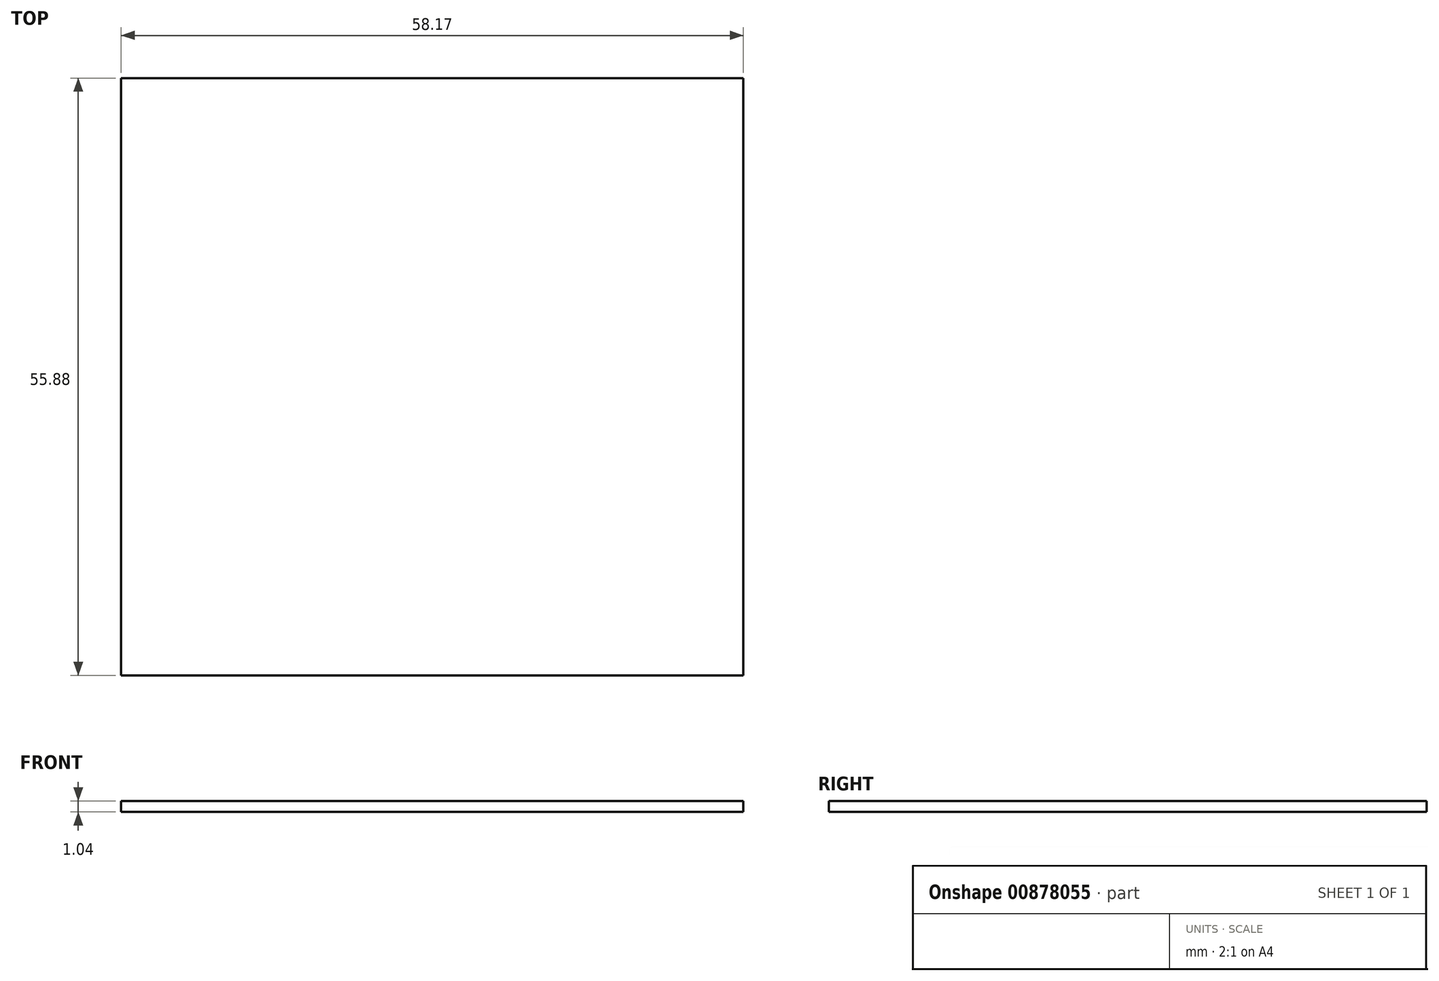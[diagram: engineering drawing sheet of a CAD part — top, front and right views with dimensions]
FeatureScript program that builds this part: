
annotation { "Feature Type Name" : "Feature", "Feature Type Description" : "" }
export const myFeature = defineFeature(function(context is Context, id is Id, definition is map)
    precondition{}
    {
        {
            var Q0;
            Q0=qCreatedBy(makeId("Top.planeOp"),FACE);
            var sketch = newSketch(context, id + "F0", { "sketchPlane" : qUnion([Q0])});
            skLineSegment(sketch, "E0.bottom", {"start": v(0, 0) * mm, "end": v(58.17, 0) * mm});
            skLineSegment(sketch, "E0.top", {"start": v(0, 55.88) * mm, "end": v(58.17, 55.88) * mm});
            skLineSegment(sketch, "E0.left", {"start": v(0, 0) * mm, "end": v(0, 55.88) * mm});
            skLineSegment(sketch, "E0.right", {"start": v(58.17, 0) * mm, "end": v(58.17, 55.88) * mm});
            skSolve(sketch);
        }
        {
            var Q0;
            Q0=makeQuery(id+"F0.imprint","IMPRINT",FACE,{"disambiguationData":[TD([[makeQuery(id+"F0.imprint","IMPRINT",EDGE,{"derivedFrom":sQuery(id+"F0.wireOp",EDGE,"E0.bottom")}),1.0]])]});
            extrude(context, id + "F1", {"entities" : qUnion([Q0]), "depth" : 1.04 * mm, "offsetDistance" : 25.4 * mm});
        }
    });
